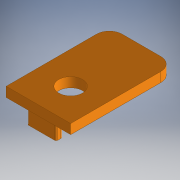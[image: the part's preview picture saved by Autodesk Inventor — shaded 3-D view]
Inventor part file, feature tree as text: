
AUTODESK INVENTOR PART (.ipt)
format: ipt  version: 2018 (Build 220112000, 112)  size: 138,240 bytes
history: native  units: mm
features: extrude x3, fillet x2, sketch x1
ambient origin geometry x8: Origin, YZ Plane, XZ Plane, XY Plane, X Axis, Y Axis, Z Axis, Center Point
bodies: Solid1 (feature_tree)
feature tree (6):
  sketch  "Sketch1"  dims[d0=20.0mm d1=32.0mm d2=0.15mm d3=0.15mm d5=7.07mm d6=12.9mm d7=13.7mm d8=22.0mm d9=3.0mm d10=0.0mm d11=3.0mm d12=0.0mm d13=4.0mm d15=5.0mm d16=0.0mm d17=0.5mm d18=2.0mm d19=2.3mm d20=9.0mm d21=9.3mm d22=0.85mm]
  extrude  "Extrusion1"  Depth=0.5mm
  extrude  "Extrusion2"  Depth=0.5mm
  fillet  "Fillet1"  Radius=22.0mm
  extrude  "Extrusion3"  Depth=3.0mm TaperAngle=0.0deg
  fillet  "Fillet2"  Radius=3.0mm
